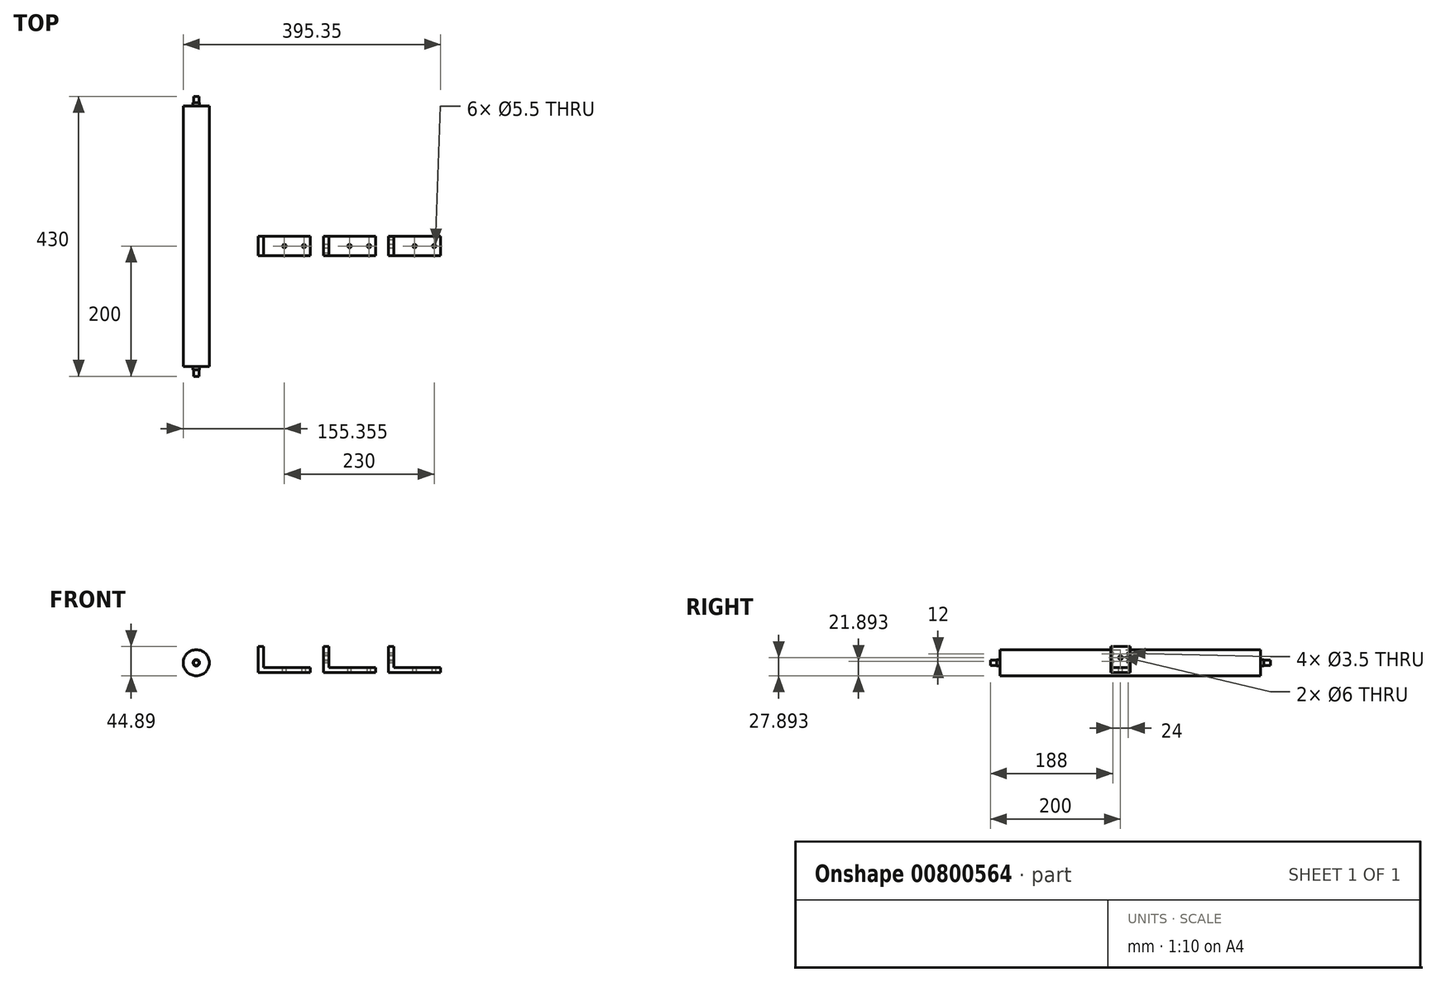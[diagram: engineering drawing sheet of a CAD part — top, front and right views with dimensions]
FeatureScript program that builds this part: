
annotation { "Feature Type Name" : "Feature", "Feature Type Description" : "" }
export const myFeature = defineFeature(function(context is Context, id is Id, definition is map)
    precondition{}
    {
        {
            var Q0;
            Q0=qCreatedBy(makeId("Front.planeOp"),FACE);
            var sketch = newSketch(context, id + "F0", { "sketchPlane" : qUnion([Q0])});
            skCircle(sketch, "E0", {"center": v(0, 0) * mm, "radius": 4 * mm});
            skSolve(sketch);
        }
        {
            var Q0;
            Q0 = qSketchRegion(id + "F0", true);
            extrude(context, id + "F1", {"entities" : qUnion([Q0]), "endBound" : BoundingType.SYMMETRIC, "depth" : 430 * mm, "offsetDistance" : 25 * mm});
        }
        {
            var Q0;
            Q0=qCreatedBy(makeId("Front.planeOp"),FACE);
            var sketch = newSketch(context, id + "F2", { "sketchPlane" : qUnion([Q0])});
            skCircle(sketch, "E1", {"center": v(0, 0) * mm, "radius": 5 * mm});
            skSolve(sketch);
        }
        {
            var Q0;
            Q0 = qSketchRegion(id + "F2", true);
            extrude(context, id + "F3", {"entities" : qUnion([Q0]), "operationType" : NewBodyOperationType.ADD, "endBound" : BoundingType.SYMMETRIC, "depth" : 410 * mm, "offsetDistance" : 25 * mm});
        }
        {
            var Q0;
            Q0=qCreatedBy(makeId("Front.planeOp"),FACE);
            var sketch = newSketch(context, id + "F4", { "sketchPlane" : qUnion([Q0])});
            skCircle(sketch, "E2", {"center": v(0, 0) * mm, "radius": 20 * mm});
            skSolve(sketch);
        }
        {
            var Q0;
            Q0 = qSketchRegion(id + "F4", true);
            extrude(context, id + "F5", {"entities" : qUnion([Q0]), "operationType" : NewBodyOperationType.ADD, "endBound" : BoundingType.SYMMETRIC, "depth" : 400 * mm, "offsetDistance" : 25 * mm});
        }
        {
            var Q0;
            Q0=qCreatedBy(makeId("Front.planeOp"),FACE);
            var sketch = newSketch(context, id + "F6", { "sketchPlane" : qUnion([Q0])});
            skLineSegment(sketch, "E3", {"start": v(95.35, 24.9) * mm, "end": v(95.35, -15.1) * mm});
            skLineSegment(sketch, "E4", {"start": v(95.35, -15.1) * mm, "end": v(175.35, -15.1) * mm});
            skLineSegment(sketch, "E5", {"start": v(175.35, -15.1) * mm, "end": v(175.35, -7.1) * mm});
            skLineSegment(sketch, "E6", {"start": v(175.35, -7.1) * mm, "end": v(103.35, -7.1) * mm});
            skLineSegment(sketch, "E7", {"start": v(103.35, -7.1) * mm, "end": v(103.35, 24.9) * mm});
            skLineSegment(sketch, "E8", {"start": v(103.35, 24.9) * mm, "end": v(95.35, 24.9) * mm});
            skSolve(sketch);
        }
        {
            var Q0;
            Q0 = qSketchRegion(id + "F6", true);
            extrude(context, id + "F7", {"entities" : qUnion([Q0]), "depth" : 30 * mm, "offsetDistance" : 25 * mm});
        }
        {
            var Q0;
            Q0=makeQuery(id+"F7.opExtrude","SWEPT_FACE",FACE,{"disambiguationData":[OSD([sQuery(id+"F6.wireOp",EDGE,"E6")])]});
            var sketch = newSketch(context, id + "F8", { "sketchPlane" : qUnion([Q0])});
            skCircle(sketch, "E9", {"center": v(135.35, -15) * mm, "radius": 2.75 * mm});
            skCircle(sketch, "E10", {"center": v(165.35, -15) * mm, "radius": 2.75 * mm});
            skLineSegment(sketch, "E11", {"start": v(175.35, -15) * mm, "end": v(103.35, -15) * mm, "construction": true});
            skSolve(sketch);
        }
        {
            var Q0;
            Q0 = qSketchRegion(id + "F8", true);
            extrude(context, id + "F9", {"entities" : qUnion([Q0]), "operationType" : NewBodyOperationType.REMOVE, "endBound" : BoundingType.THROUGH_ALL, "oppositeDirection" : true, "depth" : 25 * mm, "offsetDistance" : 25 * mm});
        }
        {
            var Q0;
            Q0=makeQuery(id+"F7.opExtrude","SWEPT_FACE",FACE,{"disambiguationData":[OSD([sQuery(id+"F6.wireOp",EDGE,"E7")])]});
            var sketch = newSketch(context, id + "F10", { "sketchPlane" : qUnion([Q0])});
            skCircle(sketch, "E12", {"center": v(-15, 15.64) * mm, "radius": 1.75 * mm});
            skLineSegment(sketch, "E13", {"start": v(-15, 24.9) * mm, "end": v(-15, -7.1) * mm, "construction": true});
            skLineSegment(sketch, "E14", {"start": v(-18.74, 7.9) * mm, "end": v(-10.32, 7.9) * mm, "construction": true});
            skCircle(sketch, "E15.MirrorC", {"center": v(-15, 0.14) * mm, "radius": 1.75 * mm});
            skSolve(sketch);
        }
        {
            var Q0;
            Q0=makeQuery(id+"F7.opExtrude","SWEPT_BODY",BODY,{"disambiguationData":[OSD([sQuery(id+"F6.wireOp",EDGE,"E3"),sQuery(id+"F6.wireOp",EDGE,"E4"),sQuery(id+"F6.wireOp",EDGE,"E5"),sQuery(id+"F6.wireOp",EDGE,"E6"),sQuery(id+"F6.wireOp",EDGE,"E7"),sQuery(id+"F6.wireOp",EDGE,"E8")])]});
            transform(context, id + "F11", {"entities" : qUnion([Q0]), "transformType" : TransformType.TRANSLATION_3D, "dx" : 100 * mm, "dy" : 0 * mm, "dz" : 0 * mm, "makeCopy" : true});
        }
        {
            var Q0;
            Q0=makeQuery(id+"F11.opPattern","COPY",BODY,{"derivedFrom":makeQuery(id+"F7.opExtrude","SWEPT_BODY",BODY,{"disambiguationData":[OSD([sQuery(id+"F6.wireOp",EDGE,"E3"),sQuery(id+"F6.wireOp",EDGE,"E4"),sQuery(id+"F6.wireOp",EDGE,"E5"),sQuery(id+"F6.wireOp",EDGE,"E6"),sQuery(id+"F6.wireOp",EDGE,"E7"),sQuery(id+"F6.wireOp",EDGE,"E8")])]}),"instanceName":"1"});
            transform(context, id + "F12", {"entities" : qUnion([Q0]), "transformType" : TransformType.TRANSLATION_3D, "dx" : 100 * mm, "dy" : 0 * mm, "dz" : 0 * mm, "makeCopy" : true});
        }
        {
            var Q0;
            Q0=makeQuery(id+"F11.opPattern","COPY",FACE,{"derivedFrom":makeQuery(id+"F7.opExtrude","SWEPT_FACE",FACE,{"disambiguationData":[OSD([sQuery(id+"F6.wireOp",EDGE,"E7")])]}),"instanceName":"1"});
            var sketch = newSketch(context, id + "F13", { "sketchPlane" : qUnion([Q0])});
            skLineSegment(sketch, "E16", {"start": v(-27, 24.9) * mm, "end": v(-27, -7.1) * mm, "construction": true});
            skCircle(sketch, "E17", {"center": v(-27, 13.9) * mm, "radius": 1.75 * mm});
            skLineSegment(sketch, "E18", {"start": v(-28.1, 7.9) * mm, "end": v(-25.18, 7.9) * mm, "construction": true});
            skCircle(sketch, "E19.MirrorC", {"center": v(-27, 1.9) * mm, "radius": 1.75 * mm});
            skCircle(sketch, "E20", {"center": v(-15, 7.9) * mm, "radius": 3 * mm});
            skLineSegment(sketch, "E21", {"start": v(-15, 24.9) * mm, "end": v(-15, -7.1) * mm, "construction": true});
            skSolve(sketch);
        }
        {
            var Q0;
            Q0 = qSketchRegion(id + "F13", true);
            extrude(context, id + "F14", {"entities" : qUnion([Q0]), "operationType" : NewBodyOperationType.REMOVE, "oppositeDirection" : true, "depth" : 8 * mm, "offsetDistance" : 25 * mm});
        }
        {
            var Q0;
            Q0=makeQuery(id+"F12.opPattern","COPY",FACE,{"derivedFrom":makeQuery(id+"F11.opPattern","COPY",FACE,{"derivedFrom":makeQuery(id+"F7.opExtrude","SWEPT_FACE",FACE,{"disambiguationData":[OSD([sQuery(id+"F6.wireOp",EDGE,"E7")])]}),"instanceName":"1"}),"instanceName":"1"});
            var sketch = newSketch(context, id + "F15", { "sketchPlane" : qUnion([Q0])});
            skLineSegment(sketch, "E22", {"start": v(-3, 24.9) * mm, "end": v(-3, -7.1) * mm, "construction": true});
            skCircle(sketch, "E23", {"center": v(-3, 13.9) * mm, "radius": 1.75 * mm});
            skLineSegment(sketch, "E24", {"start": v(-4.51, 7.9) * mm, "end": v(3.42, 7.9) * mm, "construction": true});
            skCircle(sketch, "E25.MirrorC", {"center": v(-3, 1.9) * mm, "radius": 1.75 * mm});
            skLineSegment(sketch, "E26", {"start": v(-15, 24.9) * mm, "end": v(-15, -7.1) * mm, "construction": true});
            skCircle(sketch, "E27", {"center": v(-15, 7.9) * mm, "radius": 3 * mm});
            skSolve(sketch);
        }
        {
            var Q0;
            Q0 = qSketchRegion(id + "F15", true);
            extrude(context, id + "F16", {"entities" : qUnion([Q0]), "operationType" : NewBodyOperationType.REMOVE, "oppositeDirection" : true, "depth" : 8 * mm, "offsetDistance" : 25 * mm});
        }
    });
